# Revit family: Haworth_BuzziJet_Pendant
name_source: partatom
category: Lighting Fixtures
revit_build: Autodesk Revit 2018 (Build: 20170223_1515(x64)
units: mm (PartAtom-declared; Revit-internal decimal feet)

## family parameters
Cut with Voids When Loaded = No
Host = Face
Light Source = No
Part Type = Normal
Room Calculation Point = No
Round Connector Dimension = Use Diameter
Shared = No

## types (4) — shared parameters
Actual Depth = 31.5 "
Actual Width = 31.5 "
Assembly Code = E2020200
Glass Finish = Haworth _ Glass _ Frosted
Manufacturer = Haworth
Max. Cable Length = 196.85 "
Min. Cable Length = 20 "
Model = HCBZ-JTP
Note = Verify Final Dim. w/ Haworth
Revision = 1
Split Cable Length = 15.75 "
Trim Finish = Haworth _ Paint _ Collection Black
URL = http://www.haworth.com
URL - Product = https://www.haworth.com
Warranty = http://www.haworth.com
zero-valued in all types: Default Elevation

## per-type parameters (varying)
| type | Actual Height | Description | Medium | Small | Split Cable | Straight Cable |
| HCBZ-JTP2 - Medium Pendant - Split Cable | 17.72 " | Haworth BuzziJet Medium Pendant Light Split Cable | Yes | No | Yes | No |
| HCBZ-JTP2 - Medium Pendant - Straight Cable | 17.72 " | Haworth BuzziJet Medium Pendant Light Straight Cable | Yes | No | No | Yes |
| HCBZ-JTP1 - Small Pendant - Split Cable | 8.86 " | Haworth BuzziJet Small Pendant Light Split Cable | No | Yes | Yes | No |
| HCBZ-JTP1 - Small Pendant - Straight Cable | 8.86 " | Haworth BuzziJet Small Pendant Light Straight Cable | No | Yes | No | Yes |

## geometry (parser evidence)
native form markers: Sweep x5
no freeform markers — native parametric forms only
